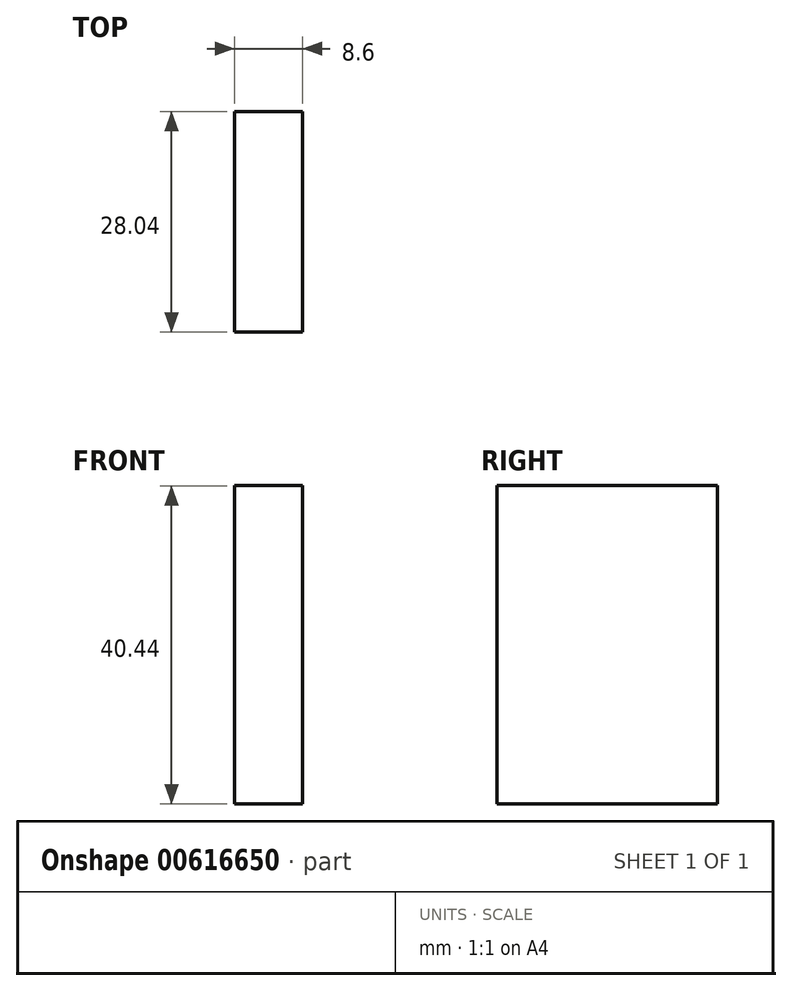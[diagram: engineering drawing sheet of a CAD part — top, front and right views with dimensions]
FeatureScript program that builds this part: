
annotation { "Feature Type Name" : "Feature", "Feature Type Description" : "" }
export const myFeature = defineFeature(function(context is Context, id is Id, definition is map)
    precondition{}
    {
        {
            var Q0;
            Q0=qCreatedBy(makeId("Right.planeOp"),FACE);
            var sketch = newSketch(context, id + "F0", { "sketchPlane" : qUnion([Q0])});
            skLineSegment(sketch, "E0.bottom", {"start": v(-44.3, 55.5) * mm, "end": v(62.87, 55.5) * mm});
            skLineSegment(sketch, "E0.top", {"start": v(-44.3, -58.78) * mm, "end": v(62.87, -58.78) * mm});
            skLineSegment(sketch, "E0.left", {"start": v(-44.3, 55.5) * mm, "end": v(-44.3, -58.78) * mm});
            skLineSegment(sketch, "E0.right", {"start": v(62.87, 55.5) * mm, "end": v(62.87, -58.78) * mm});
            skLineSegment(sketch, "E1.bottom", {"start": v(-44.3, 55.5) * mm, "end": v(-14.69, 55.5) * mm});
            skLineSegment(sketch, "E1.top", {"start": v(-44.3, 23.91) * mm, "end": v(-14.69, 23.91) * mm});
            skLineSegment(sketch, "E1.left", {"start": v(-44.3, 55.5) * mm, "end": v(-44.3, 23.91) * mm});
            skLineSegment(sketch, "E1.right", {"start": v(-14.69, 55.5) * mm, "end": v(-14.69, 23.91) * mm});
            skLineSegment(sketch, "E2.bottom", {"start": v(-14.69, 23.91) * mm, "end": v(13.35, 23.91) * mm});
            skLineSegment(sketch, "E2.top", {"start": v(-14.69, -16.53) * mm, "end": v(13.35, -16.53) * mm});
            skLineSegment(sketch, "E2.left", {"start": v(-14.69, 23.91) * mm, "end": v(-14.69, -16.53) * mm});
            skLineSegment(sketch, "E2.right", {"start": v(13.35, 23.91) * mm, "end": v(13.35, -16.53) * mm});
            skLineSegment(sketch, "E3.bottom", {"start": v(13.35, -16.94) * mm, "end": v(62.87, -16.94) * mm});
            skLineSegment(sketch, "E3.top", {"start": v(13.35, -58.78) * mm, "end": v(62.87, -58.78) * mm});
            skLineSegment(sketch, "E3.left", {"start": v(13.35, -16.94) * mm, "end": v(13.35, -58.78) * mm});
            skLineSegment(sketch, "E3.right", {"start": v(62.87, -16.94) * mm, "end": v(62.87, -58.78) * mm});
            skSolve(sketch);
        }
        {
            var Q0;
            Q0=makeQuery(id+"F0.imprint","IMPRINT",FACE,{"disambiguationData":[TD([[makeQuery(id+"F0.imprint","IMPRINT",EDGE,{"derivedFrom":sQuery(id+"F0.wireOp",EDGE,"E2.bottom")}),-1.0]])]});
            var Q1;
            Q1=makeQuery(id+"F0.imprint","IMPRINT",FACE,{"disambiguationData":[TD([[makeQuery(id+"F0.imprint","IMPRINT",EDGE,{"derivedFrom":sQuery(id+"F0.wireOp",EDGE,"E1.bottom")}),-1.0]])]});
            extrude(context, id + "F1", {"entities" : qUnion([Q0, Q1]), "depth" : 8.6 * mm, "offsetDistance" : 25 * mm});
        }
    });
